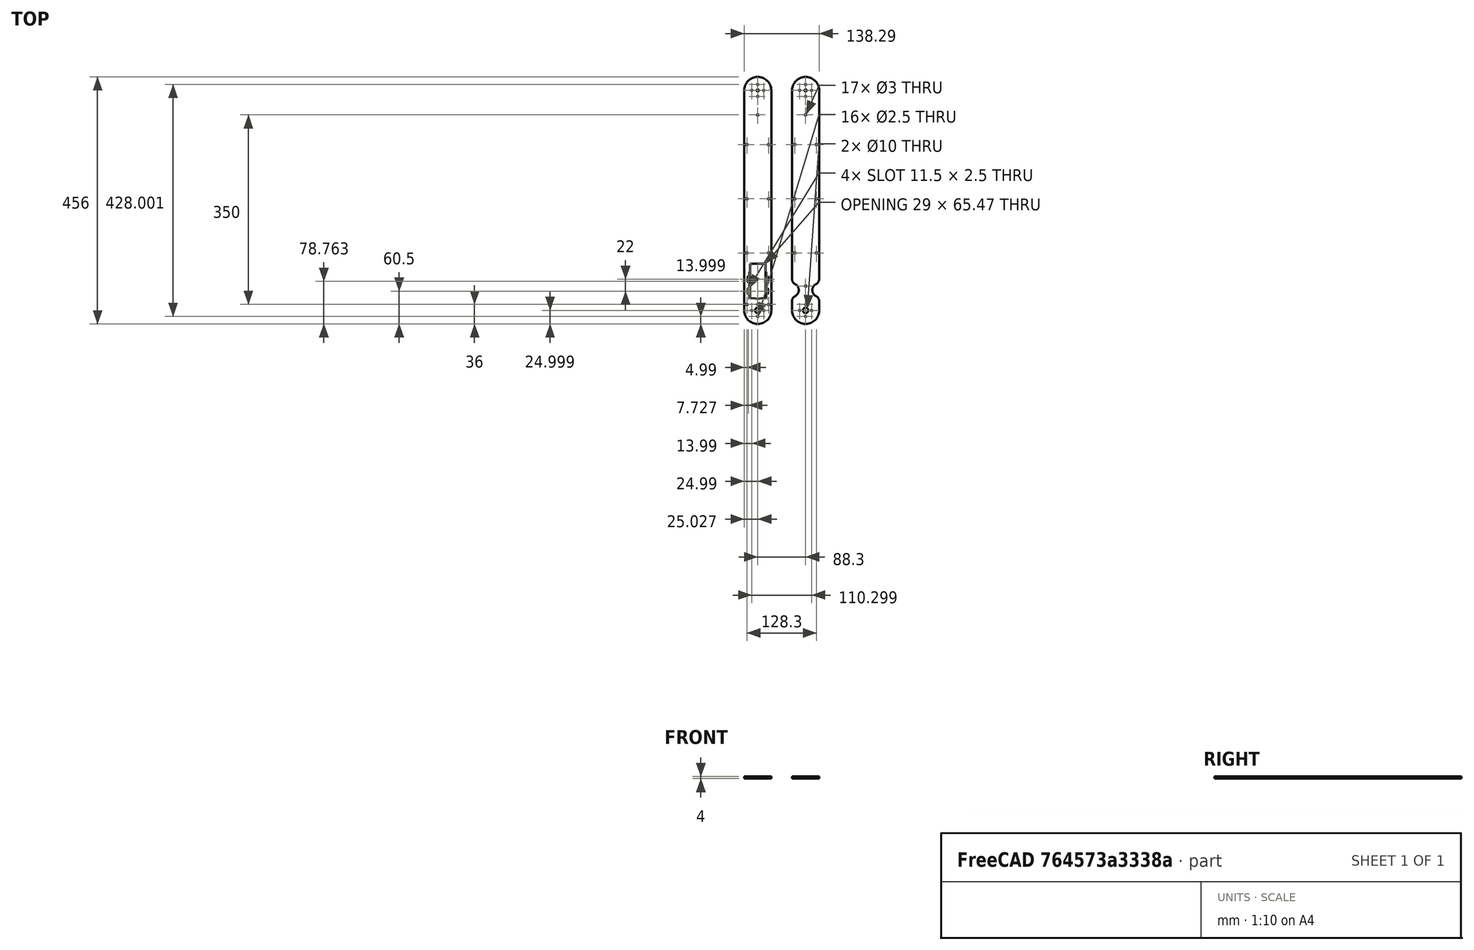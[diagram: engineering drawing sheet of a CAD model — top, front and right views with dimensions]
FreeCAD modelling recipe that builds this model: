
FCSTD DOCUMENT  (FreeCAD 1.0R39109 (Git))
Label: arm_assembly_def3
License: All rights reserved
LicenseURL: https://en.wikipedia.org/wiki/All_rights_reserved
objects: Sketcher::SketchObject×4, PartDesign::Pad×2, PartDesign::Pocket×2, PartDesign::Body×2, Assembly::JointGroup×1, Assembly::AssemblyObject×1, PartDesign::Fillet×1
note: 25 computed .brp shape members not serialized (recipe doc carries the construction recipe); baked Part::Feature solids carry a one-line shape summary decoded from their .brp

FEATURE [Sketcher::SketchObject] Sketch
  ArcFitTolerance = 1e-06
  AttachmentSupport = -> [XY_Plane]
  FullyConstrained = false
  MakeInternals = false
  MapMode = 5
  sketch-geometry (103):
    g0: LineSegment [constr] StartX=1.5008e-12 StartY=20 StartZ=0 EndX=1.5008e-12 EndY=-20 EndZ=0
    g1: LineSegment [constr] StartX=0 StartY=0 StartZ=0 EndX=0 EndY=400 EndZ=0
    g2: LineSegment [constr] StartX=1.5008e-12 StartY=20 StartZ=0 EndX=1.5008e-12 EndY=25 EndZ=0
    g3: Circle CenterX=0 CenterY=400 CenterZ=0 NormalX=0 NormalY=0 NormalZ=1 AngleXU=0 Radius=2
    g4: Circle CenterX=-10.9997 CenterY=400 CenterZ=0 NormalX=0 NormalY=0 NormalZ=1 AngleXU=0 Radius=1.25
    g5: Circle CenterX=0 CenterY=389 CenterZ=0 NormalX=0 NormalY=0 NormalZ=1 AngleXU=0 Radius=1.25
    g6: Circle CenterX=10.9997 CenterY=400 CenterZ=0 NormalX=0 NormalY=0 NormalZ=1 AngleXU=0 Radius=1.25
    g7: Circle CenterX=0 CenterY=411 CenterZ=0 NormalX=0 NormalY=0 NormalZ=1 AngleXU=0 Radius=1.25
    g8: LineSegment [constr] StartX=0 StartY=-5 StartZ=0 EndX=0 EndY=5.99996 EndZ=0
    g9: LineSegment [constr] StartX=0 StartY=0 StartZ=0 EndX=25.23 EndY=0 EndZ=0
    g10: LineSegment [constr] StartX=0 StartY=0 StartZ=0 EndX=-25 EndY=0 EndZ=0
    g11: LineSegment [constr] StartX=20.1368 StartY=86.1259 StartZ=0 EndX=20.1368 EndY=25.0259 EndZ=0
    g12: LineSegment [constr] StartX=0.036848 StartY=80.5 StartZ=0 EndX=14.5368 EndY=80.5 EndZ=0
    g13: LineSegment StartX=14.5368 StartY=80.5 StartZ=0 EndX=-14.4632 EndY=80.5 EndZ=0
    g14: LineSegment StartX=14.5368 StartY=80.5 StartZ=0 EndX=14.5368 EndY=25.0259 EndZ=0
    g15: Circle [constr] CenterX=17.3368 CenterY=78 CenterZ=0 NormalX=0 NormalY=0 NormalZ=1 AngleXU=0 Radius=1.25
    g16: LineSegment [constr] StartX=-20.0632 StartY=86.1259 StartZ=0 EndX=20.1368 EndY=86.1259 EndZ=0
    g17: Circle [constr] CenterX=17.3368 CenterY=56.0002 CenterZ=0 NormalX=0 NormalY=0 NormalZ=1 AngleXU=0 Radius=1.25
    g18: Circle [constr] CenterX=17.3368 CenterY=34 CenterZ=0 NormalX=0 NormalY=0 NormalZ=1 AngleXU=0 Radius=1.25
    g19: Circle [constr] CenterX=0.0368605 CenterY=38.0259 CenterZ=0 NormalX=0 NormalY=0 NormalZ=1 AngleXU=0 Radius=14
    g20: ArcOfCircle [constr] CenterX=0.0368605 CenterY=38.0259 CenterZ=0 NormalX=0 NormalY=0 NormalZ=1 AngleXU=0 Radius=14 StartAngle=4.33213 EndAngle=5.09264
    g21: LineSegment [constr] StartX=5.23308 StartY=25.0259 StartZ=0 EndX=14.5368 EndY=25.0259 EndZ=0
    g22: LineSegment [constr] StartX=14.5368 StartY=25.0259 StartZ=0 EndX=20.1368 EndY=25.0259 EndZ=0
    g23: LineSegment [constr] StartX=17.3368 StartY=56.0002 StartZ=0 EndX=-17.2632 EndY=56.0002 EndZ=0
    g24: LineSegment [constr] StartX=-20.0632 StartY=25.0259 StartZ=0 EndX=-20.0632 EndY=86.1259 EndZ=0
    g25: LineSegment StartX=-14.4632 StartY=80.5 StartZ=0 EndX=-14.4632 EndY=25.0259 EndZ=0
    g26: Circle [constr] CenterX=-17.2632 CenterY=78 CenterZ=0 NormalX=0 NormalY=0 NormalZ=1 AngleXU=0 Radius=1.25
    g27: Circle [constr] CenterX=-17.2632 CenterY=56.0002 CenterZ=0 NormalX=0 NormalY=0 NormalZ=1 AngleXU=0 Radius=1.25
    g28: Circle [constr] CenterX=-17.2632 CenterY=34 CenterZ=0 NormalX=0 NormalY=0 NormalZ=1 AngleXU=0 Radius=1.25
    g29: LineSegment [constr] StartX=-14.4632 StartY=25.0259 StartZ=0 EndX=-5.15937 EndY=25.0259 EndZ=0
    g30: LineSegment [constr] StartX=-20.0632 StartY=25.0259 StartZ=0 EndX=-14.4632 EndY=25.0259 EndZ=0
    g31: LineSegment [constr] StartX=25.23 StartY=199.98 StartZ=0 EndX=-25 EndY=199.98 EndZ=0
    g32: LineSegment [constr] StartX=25.23 StartY=199.98 StartZ=0 EndX=55.23 EndY=199.98 EndZ=0
    g33: LineSegment [constr] StartX=25.23 StartY=0 StartZ=0 EndX=55.23 EndY=0 EndZ=0
    g34: LineSegment [constr] StartX=55.23 StartY=0 StartZ=0 EndX=55.23 EndY=199.98 EndZ=0
    g35: LineSegment [constr] StartX=55.23 StartY=99.9898 StartZ=0 EndX=25.23 EndY=99.9898 EndZ=0
    g36: LineSegment [constr] StartX=25.23 StartY=99.9898 StartZ=0 EndX=-25 EndY=99.9898 EndZ=0
    g37: LineSegment [constr] StartX=25.23 StartY=399.959 StartZ=0 EndX=55.23 EndY=399.959 EndZ=0
    g38: LineSegment [constr] StartX=55.23 StartY=399.959 StartZ=0 EndX=55.23 EndY=199.98 EndZ=0
    g39: LineSegment [constr] StartX=55.23 StartY=299.969 StartZ=0 EndX=25.23 EndY=299.969 EndZ=0
    g40: LineSegment [constr] StartX=25.23 StartY=299.969 StartZ=0 EndX=-25 EndY=299.969 EndZ=0
    g41: LineSegment [constr] StartX=-25 StartY=299.969 StartZ=0 EndX=-20 EndY=299.969 EndZ=0
    g42: LineSegment [constr] StartX=-20 StartY=299.969 StartZ=0 EndX=-20 EndY=199.98 EndZ=0
    g43: LineSegment [constr] StartX=-20 StartY=199.98 StartZ=0 EndX=-20 EndY=99.9898 EndZ=0
    g44: LineSegment [constr] StartX=25.23 StartY=299.969 StartZ=0 EndX=20.23 EndY=299.969 EndZ=0
    g45: LineSegment [constr] StartX=20.23 StartY=299.969 StartZ=0 EndX=20.23 EndY=199.98 EndZ=0
    g46: LineSegment [constr] StartX=20.23 StartY=199.98 StartZ=0 EndX=20.23 EndY=99.9898 EndZ=0
    g47: Circle CenterX=-20 CenterY=299.969 CenterZ=0 NormalX=0 NormalY=0 NormalZ=1 AngleXU=0 Radius=1.5
    g48: Circle CenterX=20.23 CenterY=299.969 CenterZ=0 NormalX=0 NormalY=0 NormalZ=1 AngleXU=0 Radius=1.5
    g49: Circle CenterX=-20 CenterY=199.98 CenterZ=0 NormalX=0 NormalY=0 NormalZ=1 AngleXU=0 Radius=1.5
    g50: Circle CenterX=20.23 CenterY=199.98 CenterZ=0 NormalX=0 NormalY=0 NormalZ=1 AngleXU=0 Radius=1.5
    g51: Circle CenterX=-20 CenterY=99.9898 CenterZ=0 NormalX=0 NormalY=0 NormalZ=1 AngleXU=0 Radius=1.5
    g52: Circle CenterX=20.23 CenterY=99.9898 CenterZ=0 NormalX=0 NormalY=0 NormalZ=1 AngleXU=0 Radius=1.5
    g53: LineSegment [constr] StartX=-17.2632 StartY=34 StartZ=0 EndX=17.3368 EndY=34 EndZ=0
    g54: LineSegment [constr] StartX=-17.2632 StartY=34 StartZ=0 EndX=-17.2632 EndY=25 EndZ=0
    g55: LineSegment [constr] StartX=17.3368 StartY=34 StartZ=0 EndX=17.3368 EndY=25 EndZ=0
    g56: LineSegment [constr] StartX=-17.2632 StartY=78 StartZ=0 EndX=17.3368 EndY=78 EndZ=0
    g57: LineSegment [constr] StartX=-17.2632 StartY=78 StartZ=0 EndX=-17.2632 EndY=69 EndZ=0
    g58: LineSegment [constr] StartX=17.3368 StartY=78 StartZ=0 EndX=17.3368 EndY=69 EndZ=0
    g59: LineSegment StartX=-14.4632 StartY=25.0259 StartZ=0 EndX=-14.4632 EndY=22.0259 EndZ=0
    g60: LineSegment StartX=14.5368 StartY=25.0259 StartZ=0 EndX=14.5368 EndY=22.0259 EndZ=0
    g61: LineSegment [constr] StartX=-17.2632 StartY=56.0002 StartZ=0 EndX=-17.2632 EndY=47.0002 EndZ=0
    g62: LineSegment [constr] StartX=17.3368 StartY=56.0002 StartZ=0 EndX=17.3368 EndY=47.0002 EndZ=0
    g63: Circle [constr] CenterX=0.010165 CenterY=399.952 CenterZ=0 NormalX=0 NormalY=0 NormalZ=1 AngleXU=0 Radius=25.1076
    g64: LineSegment [constr] StartX=0 StartY=400 StartZ=0 EndX=0 EndY=374.844 EndZ=0
    g65: LineSegment [constr] StartX=0 StartY=374.844 StartZ=0 EndX=0 EndY=364.844 EndZ=0
    g66: Circle [constr] CenterX=0 CenterY=364.844 CenterZ=0 NormalX=0 NormalY=0 NormalZ=1 AngleXU=0 Radius=1.5
    g67: Circle [constr] CenterX=-17.2632 CenterY=69 CenterZ=0 NormalX=0 NormalY=0 NormalZ=1 AngleXU=0 Radius=1.25
    g68: Circle [constr] CenterX=17.3368 CenterY=69 CenterZ=0 NormalX=0 NormalY=0 NormalZ=1 AngleXU=0 Radius=1.25
    g69: ArcOfCircle CenterX=-17.2632 CenterY=56.0002 CenterZ=0 NormalX=0 NormalY=0 NormalZ=1 AngleXU=0 Radius=1.25 StartAngle=3.144e-13 EndAngle=3.14159
    g70: ArcOfCircle CenterX=-17.2632 CenterY=47.0002 CenterZ=0 NormalX=0 NormalY=0 NormalZ=1 AngleXU=0 Radius=1.25 StartAngle=3.14159 EndAngle=6.28319
    g71: LineSegment StartX=-16.0132 StartY=56.0002 StartZ=0 EndX=-16.0132 EndY=47.0002 EndZ=0
    g72: LineSegment StartX=-18.5132 StartY=56.0002 StartZ=0 EndX=-18.5132 EndY=47.0002 EndZ=0
    g73: ArcOfCircle CenterX=17.3368 CenterY=34 CenterZ=0 NormalX=0 NormalY=0 NormalZ=1 AngleXU=0 Radius=1.25 StartAngle=6e-16 EndAngle=3.14159
    g74: ArcOfCircle CenterX=17.3368 CenterY=25 CenterZ=0 NormalX=0 NormalY=0 NormalZ=1 AngleXU=0 Radius=1.25 StartAngle=3.14159 EndAngle=6.28319
    g75: LineSegment StartX=18.5868 StartY=34 StartZ=0 EndX=18.5868 EndY=25 EndZ=0
    g76: LineSegment StartX=16.0868 StartY=34 StartZ=0 EndX=16.0868 EndY=25 EndZ=0
    g77: LineSegment StartX=5.233 StartY=16.0259 StartZ=0 EndX=14.5368 EndY=16.0259 EndZ=0
    g78: ArcOfCircle CenterX=0.036848 CenterY=29.0259 CenterZ=0 NormalX=0 NormalY=0 NormalZ=1 AngleXU=0 Radius=14 StartAngle=4.33214 EndAngle=5.09264
    g79: LineSegment StartX=-5.15931 StartY=16.0259 StartZ=0 EndX=-14.4632 EndY=16.0259 EndZ=0
    g80: LineSegment StartX=-14.4632 StartY=22.0259 StartZ=0 EndX=-14.4632 EndY=16.0259 EndZ=0
    g81: LineSegment StartX=14.5368 StartY=22.0259 StartZ=0 EndX=14.5368 EndY=16.0259 EndZ=0
    g82: ArcOfCircle CenterX=17.3368 CenterY=56.0002 CenterZ=0 NormalX=0 NormalY=0 NormalZ=1 AngleXU=0 Radius=1.25 StartAngle=8.3e-15 EndAngle=3.14159
    g83: ArcOfCircle CenterX=17.3368 CenterY=47.0002 CenterZ=0 NormalX=0 NormalY=0 NormalZ=1 AngleXU=0 Radius=1.25 StartAngle=3.14159 EndAngle=6.28319
    g84: LineSegment StartX=18.5868 StartY=56.0002 StartZ=0 EndX=18.5868 EndY=47.0002 EndZ=0
    g85: LineSegment StartX=16.0868 StartY=56.0002 StartZ=0 EndX=16.0868 EndY=47.0002 EndZ=0
    g86: ArcOfCircle CenterX=-17.2632 CenterY=34 CenterZ=0 NormalX=0 NormalY=0 NormalZ=1 AngleXU=0 Radius=1.25 StartAngle=1e-16 EndAngle=3.14159
    g87: ArcOfCircle CenterX=-17.2632 CenterY=25 CenterZ=0 NormalX=0 NormalY=0 NormalZ=1 AngleXU=0 Radius=1.25 StartAngle=3.14159 EndAngle=6.28319
    g88: LineSegment StartX=-16.0132 StartY=34 StartZ=0 EndX=-16.0132 EndY=25 EndZ=0
    g89: LineSegment StartX=-18.5132 StartY=34 StartZ=0 EndX=-18.5132 EndY=25 EndZ=0
    g90: Circle [constr] CenterX=0 CenterY=-6 CenterZ=0 NormalX=0 NormalY=0 NormalZ=1 AngleXU=0 Radius=14
    g91: Circle [constr] CenterX=0.010165 CenterY=-5.99291 CenterZ=0 NormalX=0 NormalY=0 NormalZ=1 AngleXU=0 Radius=11
    g92: Circle CenterX=0 CenterY=-6 CenterZ=0 NormalX=0 NormalY=0 NormalZ=1 AngleXU=0 Radius=5
    g93: Circle CenterX=0 CenterY=-16.9997 CenterZ=0 NormalX=0 NormalY=0 NormalZ=1 AngleXU=0 Radius=1.25
    g94: Circle CenterX=10.9997 CenterY=-6 CenterZ=0 NormalX=0 NormalY=0 NormalZ=1 AngleXU=0 Radius=1.25
    g95: Circle CenterX=-10.9997 CenterY=-6 CenterZ=0 NormalX=0 NormalY=0 NormalZ=1 AngleXU=0 Radius=1.25
    g96: Circle CenterX=0 CenterY=4.99996 CenterZ=0 NormalX=0 NormalY=0 NormalZ=1 AngleXU=0 Radius=1.25
    g97: ArcOfCircle CenterX=0.010165 CenterY=-5.99291 CenterZ=0 NormalX=0 NormalY=0 NormalZ=1 AngleXU=0 Radius=25 StartAngle=3.14159 EndAngle=6.28319
    g98: ArcOfCircle CenterX=0.010165 CenterY=399.952 CenterZ=0 NormalX=0 NormalY=0 NormalZ=1 AngleXU=0 Radius=25 StartAngle=0 EndAngle=3.14159
    g99: LineSegment StartX=-24.9898 StartY=-5.99291 StartZ=0 EndX=-24.9898 EndY=399.952 EndZ=0
    g100: LineSegment StartX=25.0102 StartY=-5.99291 StartZ=0 EndX=25.0102 EndY=399.952 EndZ=0
    g101: LineSegment [constr] StartX=0 StartY=364.844 StartZ=0 EndX=0 EndY=354.844 EndZ=0
    g102: Circle CenterX=0 CenterY=354.844 CenterZ=0 NormalX=0 NormalY=0 NormalZ=1 AngleXU=0 Radius=1.5
  constraints (212):
    c: Vertical(g0)
    c: Vertical(g1)
    c: Coincident(g2,g0)
    c: Vertical(g2)
    c: Diameter(g3) = 4
    c: Coincident(g3,g1)
    c: Diameter(g7) = 2.5
    c: Diameter(g4) = 2.5
    c: Diameter(g5) = 2.5
    c: Diameter(g6) = 2.5
    c: Vertical(g8)
    c: Horizontal(g10)
    c: Horizontal(g9)
    c: Coincident(g16,g11)
    c: Coincident(g24,g16)
    c: Horizontal(g16)
    c: Vertical(g11)
    c: Vertical(g24)
    c: Distance(g11,g24) = 40.2
    c: Distance(g16,g24) = 61.1
    c: Diameter(g20) = 28
    c: Horizontal(g12)
    c: Coincident(g13,g12)
    c: Horizontal(g13)
    c: Coincident(g25,g13)
    c: Vertical(g25)
    c: Coincident(g14,g12)
    c: Vertical(g14)
    c: Coincident(g19,g20)
    c: PointOnObject(g20,g19)
    c: Coincident(g21,g20)
    c: Coincident(g21,g14)
    c: Horizontal(g21)
    c: Coincident(g22,g14)
    c: Coincident(g22,g11)
    c: Horizontal(g22)
    c: Coincident(g29,g25)
    c: Coincident(g29,g20)
    c: Horizontal(g29)
    c: Coincident(g30,g24)
    c: Coincident(g30,g25)
    c: Horizontal(g30)
    c: Coincident(g23,g17)
    c: Coincident(g23,g27)
    c: Horizontal(g23)
    c: DistanceY(g19,g1) = 361.974
    c: Horizontal(g31)
    c: Distance(g32) = 30
    c: Horizontal(g32)
    c: Coincident(g32,g31)
    c: Distance(g33) = 30
    c: Horizontal(g33)
    c: Coincident(g33,g9)
    c: PointOnObject(g33,g-1)
    c: Coincident(g34,g33)
    c: Coincident(g34,g32)
    c: Vertical(g34)
    c: Symmetric(g34,g34,g35)
    c: Horizontal(g35)
    c: Coincident(g36,g35)
    c: Horizontal(g36)
    c: Distance(g37) = 30
    c: Horizontal(g37)
    c: Coincident(g38,g37)
    c: Coincident(g38,g32)
    c: Symmetric(g38,g38,g39)
    c: Horizontal(g39)
    c: Coincident(g40,g39)
    c: Horizontal(g40)
    c: Distance(g41) = 5
    c: Coincident(g41,g40)
    c: PointOnObject(g41,g40)
    c: Coincident(g42,g41)
    c: PointOnObject(g42,g31)
    c: Vertical(g42)
    c: Coincident(g43,g42)
    c: PointOnObject(g43,g36)
    c: Vertical(g43)
    c: Distance(g44) = 5
    c: Coincident(g44,g39)
    c: PointOnObject(g44,g40)
    c: Coincident(g45,g44)
    c: PointOnObject(g45,g31)
    c: Vertical(g45)
    c: Coincident(g46,g45)
    c: PointOnObject(g46,g36)
    c: Vertical(g46)
    c: Coincident(g47,g41)
    c: Diameter(g47) = 3
    c: Coincident(g48,g44)
    c: Equal(g47,g48)
    c: Coincident(g49,g42)
    c: Equal(g47,g49)
    c: Coincident(g50,g45)
    c: Equal(g49,g50)
    c: Coincident(g51,g43)
    c: Equal(g49,g51)
    c: Coincident(g52,g46)
    c: Equal(g51,g52)
    c: Coincident(g53,g28)
    c: Coincident(g53,g18)
    c: Horizontal(g53)
    c: DistanceX(g53,g53) = 34.6
    c: Coincident(g54,g28)
    c: Vertical(g54)
    c: Coincident(g55,g18)
    c: Vertical(g55)
    c: Coincident(g56,g26)
    c: Coincident(g56,g15)
    c: Horizontal(g56)
    c: DistanceX(g56,g56) = 34.6
    c: Distance(g57) = 9
    c: Coincident(g57,g26)
    c: Vertical(g57)
    c: Coincident(g58,g15)
    c: Vertical(g58)
    c: DistanceX(g25,g14) = 29
    c: Distance(g59) = 3
    c: Coincident(g59,g25)
    c: Vertical(g59)
    c: Coincident(g60,g14)
    c: Vertical(g60)
    c: DistanceX(g23,g23) = 34.6
    c: Coincident(g61,g23)
    c: Vertical(g61)
    c: Coincident(g62,g17)
    c: Vertical(g62)
    c: DistanceX(g1) = 0
    c: DistanceY(g1) = 400
    c: Coincident(g64,g1)
    c: PointOnObject(g64,g63)
    c: Vertical(g64)
    c: Distance(g65) = 10
    c: Coincident(g65,g64)
    c: PointOnObject(g65,g1)
    c: Diameter(g66) = 3
    c: Coincident(g66,g65)
    c: DistanceX(g26) = -17.2632
    c: DistanceY(g26) = 78
    c: DistanceX(g23) = -17.2632
    c: DistanceY(g23) = 56.0002
    c: Equal(g58,g57)
    c: Equal(g61,g57)
    c: Equal(g62,g61)
    c: DistanceX(g28) = -17.2632
    c: DistanceY(g28) = 34
    c: Equal(g54,g61)
    c: Equal(g55,g54)
    c: Equal(g60,g59)
    c: Coincident(g67,g57)
    c: Equal(g67,g26)
    c: Coincident(g68,g58)
    c: Equal(g68,g15)
    c: Tangent(g69,g71) = 1.5708
    c: Tangent(g69,g72) = -1.5708
    c: Tangent(g70,g71) = 1.5708
    c: Tangent(g70,g72) = -1.5708
    c: Equal(g69,g70)
    c: Coincident(g69,g23)
    c: Coincident(g70,g61)
    c: Equal(g27,g69)
    c: Tangent(g73,g75) = 1.5708
    c: Tangent(g73,g76) = -1.5708
    c: Tangent(g74,g75) = 1.5708
    c: Tangent(g74,g76) = -1.5708
    c: Equal(g73,g74)
    c: Radius(g73) = 1.25
    c: Coincident(g73,g18)
    c: Coincident(g74,g55)
    c: Diameter(g78) = 28
    c: Coincident(g77,g78)
    c: Horizontal(g77)
    c: Coincident(g79,g78)
    c: Horizontal(g79)
    c: Coincident(g80,g59)
    c: Coincident(g80,g79)
    c: Vertical(g80)
    c: Coincident(g81,g60)
    c: Coincident(g81,g77)
    c: Vertical(g81)
    c: Tangent(g82,g84) = 1.5708
    c: Tangent(g82,g85) = -1.5708
    c: Tangent(g83,g84) = 1.5708
    c: Tangent(g83,g85) = -1.5708
    c: Equal(g82,g83)
    c: Tangent(g86,g88) = 1.5708
    c: Tangent(g86,g89) = -1.5708
    c: Tangent(g87,g88) = 1.5708
    c: Tangent(g87,g89) = -1.5708
    c: Equal(g86,g87)
    c: Diameter(g90) = 28
    c: Diameter(g91) = 22
    c: Diameter(g92) = 10
    c: Coincident(g92,g90)
    c: Diameter(g96) = 2.5
    c: Diameter(g95) = 2.5
    c: Diameter(g93) = 2.5
    c: Diameter(g94) = 2.5
    c: Tangent(g97,g99) = 1.5708
    c: Tangent(g97,g100) = -1.5708
    c: Tangent(g98,g99) = 1.5708
    c: Tangent(g98,g100) = -1.5708
    c: Equal(g97,g98)
    c: Vertical(g100)
    c: Radius(g97) = 25
    c: Coincident(g97,g91)
    c: Coincident(g98,g63)
    c: Distance(g101) = 10
    c: Coincident(g101,g65)
    c: PointOnObject(g101,g1)
    c: Coincident(g102,g101)
    c: Equal(g102,g66)
FEATURE [Sketcher::SketchObject] Sketch001
  ArcFitTolerance = 1e-06
  FullyConstrained = false
  MakeInternals = false
  MapMode = 5
  sketch-geometry (50):
    g0: Circle [constr] CenterX=0 CenterY=0.000303 CenterZ=0 NormalX=0 NormalY=0 NormalZ=1 AngleXU=0 Radius=14
    g1: Circle CenterX=0 CenterY=0.000303 CenterZ=0 NormalX=0 NormalY=0 NormalZ=1 AngleXU=0 Radius=2
    g2: Circle [constr] CenterX=0 CenterY=0 CenterZ=0 NormalX=0 NormalY=0 NormalZ=1 AngleXU=0 Radius=11
    g3: Circle CenterX=10.9997 CenterY=0.000303 CenterZ=0 NormalX=0 NormalY=0 NormalZ=1 AngleXU=0 Radius=1.25
    g4: Circle CenterX=0 CenterY=11 CenterZ=0 NormalX=0 NormalY=0 NormalZ=1 AngleXU=0 Radius=1.25
    g5: Circle CenterX=-10.9997 CenterY=0.000303 CenterZ=0 NormalX=0 NormalY=0 NormalZ=1 AngleXU=0 Radius=1.25
    g6: Circle CenterX=0 CenterY=-10.9994 CenterZ=0 NormalX=0 NormalY=0 NormalZ=1 AngleXU=0 Radius=1.25
    g7: LineSegment [constr] StartX=25 StartY=200 StartZ=0 EndX=-25 EndY=200 EndZ=0
    g8: LineSegment [constr] StartX=25 StartY=200 StartZ=0 EndX=55 EndY=200 EndZ=0
    g9: LineSegment [constr] StartX=25 StartY=0 StartZ=0 EndX=55 EndY=0 EndZ=0
    g10: LineSegment [constr] StartX=55 StartY=200 StartZ=0 EndX=55 EndY=0 EndZ=0
    g11: LineSegment [constr] StartX=55 StartY=100 StartZ=0 EndX=25 EndY=100 EndZ=0
    g12: LineSegment [constr] StartX=25 StartY=100 StartZ=0 EndX=-25 EndY=100 EndZ=0
    g13: LineSegment [constr] StartX=55 StartY=300 StartZ=0 EndX=25 EndY=300 EndZ=0
    g14: LineSegment [constr] StartX=25 StartY=300 StartZ=0 EndX=-25 EndY=300 EndZ=0
    g15: LineSegment [constr] StartX=-25 StartY=300 StartZ=0 EndX=-20 EndY=300 EndZ=0
    g16: LineSegment [constr] StartX=-20 StartY=300 StartZ=0 EndX=-20 EndY=200 EndZ=0
    g17: LineSegment [constr] StartX=-20 StartY=200 StartZ=0 EndX=-20 EndY=100 EndZ=0
    g18: LineSegment [constr] StartX=25 StartY=100 StartZ=0 EndX=20 EndY=100 EndZ=0
    g19: LineSegment [constr] StartX=20 StartY=100 StartZ=0 EndX=20 EndY=200 EndZ=0
    g20: LineSegment [constr] StartX=20 StartY=200 StartZ=0 EndX=20 EndY=300 EndZ=0
    g21: Circle CenterX=-20 CenterY=300 CenterZ=0 NormalX=0 NormalY=0 NormalZ=1 AngleXU=0 Radius=1.5
    g22: Circle CenterX=20 CenterY=300 CenterZ=0 NormalX=0 NormalY=0 NormalZ=1 AngleXU=0 Radius=1.5
    g23: Circle CenterX=-20 CenterY=200 CenterZ=0 NormalX=0 NormalY=0 NormalZ=1 AngleXU=0 Radius=1.5
    g24: Circle CenterX=20 CenterY=200 CenterZ=0 NormalX=0 NormalY=0 NormalZ=1 AngleXU=0 Radius=1.5
    g25: Circle CenterX=-20 CenterY=100 CenterZ=0 NormalX=0 NormalY=0 NormalZ=1 AngleXU=0 Radius=1.5
    g26: Circle CenterX=20 CenterY=100 CenterZ=0 NormalX=0 NormalY=0 NormalZ=1 AngleXU=0 Radius=1.5
    g27: Circle [constr] CenterX=0 CenterY=0 CenterZ=0 NormalX=0 NormalY=0 NormalZ=1 AngleXU=0 Radius=25
    g28: LineSegment [constr] StartX=0 StartY=0 StartZ=0 EndX=0 EndY=25 EndZ=0
    g29: LineSegment [constr] StartX=0 StartY=25 StartZ=0 EndX=0 EndY=35 EndZ=0
    g30: Circle [constr] CenterX=0 CenterY=35 CenterZ=0 NormalX=0 NormalY=0 NormalZ=1 AngleXU=0 Radius=1.5
    g31: LineSegment [constr] StartX=0 StartY=35 StartZ=0 EndX=0 EndY=45 EndZ=0
    g32: Circle CenterX=0 CenterY=45 CenterZ=0 NormalX=0 NormalY=0 NormalZ=1 AngleXU=0 Radius=1.5
    g33: Circle CenterX=0 CenterY=406.001 CenterZ=0 NormalX=0 NormalY=0 NormalZ=1 AngleXU=0 Radius=5
    g34: Circle CenterX=0 CenterY=417.001 CenterZ=0 NormalX=0 NormalY=0 NormalZ=1 AngleXU=0 Radius=1.25
    g35: Circle CenterX=-10.9997 CenterY=406.001 CenterZ=0 NormalX=0 NormalY=0 NormalZ=1 AngleXU=0 Radius=1.25
    g36: Circle CenterX=0 CenterY=395.001 CenterZ=0 NormalX=0 NormalY=0 NormalZ=1 AngleXU=0 Radius=1.25
    g37: LineSegment [constr] StartX=0 StartY=6.0003 StartZ=0 EndX=0 EndY=406.001 EndZ=0
    g38: Circle CenterX=10.9997 CenterY=406.001 CenterZ=0 NormalX=0 NormalY=0 NormalZ=1 AngleXU=0 Radius=1.25
    g39: LineSegment [constr] StartX=25 StartY=406.001 StartZ=0 EndX=55 EndY=406.001 EndZ=0
    g40: Circle [constr] CenterX=0 CenterY=406.001 CenterZ=0 NormalX=0 NormalY=0 NormalZ=1 AngleXU=0 Radius=25
    g41: LineSegment [constr] StartX=0 StartY=406.001 StartZ=0 EndX=0 EndY=381.001 EndZ=0
    g42: LineSegment [constr] StartX=0 StartY=381.001 StartZ=0 EndX=0 EndY=371.001 EndZ=0
    g43: Circle [constr] CenterX=0 CenterY=371.001 CenterZ=0 NormalX=0 NormalY=0 NormalZ=1 AngleXU=0 Radius=1.5
    g44: LineSegment [constr] StartX=0 StartY=371.001 StartZ=0 EndX=0 EndY=361.001 EndZ=0
    g45: Circle CenterX=0 CenterY=361.001 CenterZ=0 NormalX=0 NormalY=0 NormalZ=1 AngleXU=0 Radius=1.5
    g46: ArcOfCircle CenterX=0 CenterY=0 CenterZ=0 NormalX=0 NormalY=0 NormalZ=1 AngleXU=0 Radius=25 StartAngle=3.14159 EndAngle=6.28319
    g47: ArcOfCircle CenterX=0 CenterY=406.001 CenterZ=0 NormalX=0 NormalY=0 NormalZ=1 AngleXU=0 Radius=25 StartAngle=0 EndAngle=3.14159
    g48: LineSegment StartX=-25 StartY=6.97e-14 StartZ=0 EndX=-25 EndY=406.001 EndZ=0
    g49: LineSegment StartX=25 StartY=-6.1e-15 StartZ=0 EndX=25 EndY=406.001 EndZ=0
  constraints (91):
    c: Diameter(g0) = 28
    c: Diameter(g1) = 4
    c: Coincident(g1,g0)
    c: Diameter(g2) = 22
    c: Diameter(g4) = 2.5
    c: Diameter(g5) = 2.5
    c: Diameter(g6) = 2.5
    c: Diameter(g3) = 2.5
    c: Distance(g8) = 30
    c: Horizontal(g8)
    c: Coincident(g8,g7)
    c: Distance(g9) = 30
    c: Horizontal(g9)
    c: PointOnObject(g9,g-1)
    c: Coincident(g10,g8)
    c: Coincident(g10,g9)
    c: Symmetric(g10,g10,g11)
    c: Horizontal(g11)
    c: Coincident(g12,g11)
    c: Horizontal(g12)
    c: Horizontal(g13)
    c: Coincident(g14,g13)
    c: Horizontal(g14)
    c: Distance(g15) = 5
    c: Horizontal(g15)
    c: Coincident(g15,g14)
    c: Coincident(g16,g15)
    c: PointOnObject(g16,g7)
    c: Vertical(g16)
    c: Coincident(g17,g16)
    c: PointOnObject(g17,g12)
    c: Vertical(g17)
    c: Distance(g18) = 5
    c: Horizontal(g18)
    c: Coincident(g18,g11)
    c: Coincident(g19,g18)
    c: PointOnObject(g19,g7)
    c: Vertical(g19)
    c: Coincident(g20,g19)
    c: PointOnObject(g20,g14)
    c: Vertical(g20)
    c: Diameter(g21) = 3
    c: Coincident(g21,g15)
    c: Coincident(g22,g20)
    c: Equal(g21,g22)
    c: Coincident(g23,g16)
    c: Equal(g21,g23)
    c: Coincident(g24,g19)
    c: Equal(g23,g24)
    c: Coincident(g25,g17)
    c: Equal(g23,g25)
    c: Coincident(g26,g18)
    c: Equal(g25,g26)
    c: DistanceX(g2) = 0
    c: DistanceY(g2) = 0
    c: Coincident(g28,g2)
    c: PointOnObject(g28,g27)
    c: Vertical(g28)
    c: Distance(g29) = 10
    c: Coincident(g29,g28)
    c: Diameter(g30) = 3
    c: Coincident(g30,g29)
    c: Distance(g31) = 10
    c: Coincident(g31,g29)
    c: Coincident(g32,g31)
    c: Equal(g32,g30)
    c: Vertical(g37)
    c: Coincident(g33,g37)
    c: Diameter(g34) = 2.5
    c: Diameter(g35) = 2.5
    c: Diameter(g36) = 2.5
    c: Diameter(g38) = 2.5
    c: Horizontal(g39)
    c: Coincident(g40,g37)
    c: Coincident(g41,g37)
    c: PointOnObject(g41,g40)
    c: Vertical(g41)
    c: Coincident(g42,g41)
    c: PointOnObject(g42,g37)
    c: Coincident(g44,g42)
    c: Vertical(g44)
    c: Coincident(g45,g44)
    c: Tangent(g46,g48) = 1.5708
    c: Tangent(g46,g49) = -1.5708
    c: Tangent(g47,g48) = 1.5708
    c: Tangent(g47,g49) = -1.5708
    c: Equal(g46,g47)
    c: Vertical(g49)
    c: Radius(g46) = 25
    c: Coincident(g46,g27)
    c: Coincident(g47,g33)
FEATURE [PartDesign::Pad] Pad
  Direction = (0,0,1)
  Length = 4
  Length2 = 10
  Profile = -> Sketch
  ReferenceAxis = -> Sketch [N_Axis]
  Refine = true
  Suppressed = false
  Type = 0
FEATURE [PartDesign::Pad] Pad001
  Direction = (0,0,1)
  Length = 4
  Length2 = 10
  Profile = -> Sketch001
  ReferenceAxis = -> Sketch001 [N_Axis]
  Refine = true
  Suppressed = false
  Type = 0
FEATURE [Assembly::JointGroup] Joints
FEATURE [Assembly::AssemblyObject] Assembly
  Group = -> [Joints]
  Origin = -> Origin003
  Type = Assembly
FEATURE [Sketcher::SketchObject] Sketch002
  ArcFitTolerance = 1e-06
  AttachmentSupport = -> [Pad001]
  ExternalGeometry = -> [Pad001]
  FullyConstrained = true
  MakeInternals = false
  MapMode = 5
  Placement = pos=(0,0,4) rot=(0,0,1;0rad)
  sketch-geometry (7):
    g0: Circle [constr] CenterX=0 CenterY=406.001 CenterZ=0 NormalX=0 NormalY=0 NormalZ=1 AngleXU=0 Radius=45
    g1: LineSegment [constr] StartX=0 StartY=361.001 StartZ=0 EndX=25 EndY=361.001 EndZ=0
    g2: LineSegment [constr] StartX=25 StartY=361.001 StartZ=0 EndX=25 EndY=368.584 EndZ=0
    g3: LineSegment [constr] StartX=0 StartY=361.001 StartZ=0 EndX=-25 EndY=361.001 EndZ=0
    g4: LineSegment [constr] StartX=-25 StartY=361.001 StartZ=0 EndX=-25 EndY=368.584 EndZ=0
    g5: Circle CenterX=-25 CenterY=368.584 CenterZ=0 NormalX=0 NormalY=0 NormalZ=1 AngleXU=0 Radius=12.5
    g6: Circle CenterX=25 CenterY=368.584 CenterZ=0 NormalX=0 NormalY=0 NormalZ=1 AngleXU=0 Radius=12.5
  constraints (18):
    c: Coincident(g0,g-3)
    c: PointOnObject(g-4,g0)
    c: Coincident(g1,g-4)
    c: PointOnObject(g1,g-6)
    c: Horizontal(g1)
    c: Coincident(g2,g1)
    c: PointOnObject(g2,g0)
    c: Vertical(g2)
    c: Coincident(g3,g1)
    c: PointOnObject(g3,g-5)
    c: Horizontal(g3)
    c: Coincident(g4,g3)
    c: PointOnObject(g4,g0)
    c: Vertical(g4)
    c: Coincident(g5,g4)
    c: Diameter(g5) = 25
    c: Coincident(g6,g2)
    c: Equal(g6,g5)
FEATURE [PartDesign::Pocket] Pocket
  BaseFeature = -> Pad001
  Direction = (0,0,-1)
  Length = 11
  Length2 = 5
  Profile = -> Sketch002
  ReferenceAxis = -> Sketch002 [N_Axis]
  Refine = true
  Suppressed = false
  Type = 0
FEATURE [PartDesign::Fillet] Fillet
  Base = -> Pocket [Edge59,Edge9,Edge61,Edge6]
  BaseFeature = -> Pocket
  Radius = 10
  Refine = true
  SupportTransform = false
  Suppressed = false
  UseAllEdges = false
FEATURE [PartDesign::Body] Body001  label="arm_high_1"
  AllowCompound = false
  Group = -> [Sketch001,Pad001,Sketch002,Pocket,Fillet]
  Origin = -> Origin001
  Placement = pos=(68.48,410,17.66) rot=(0,0,1;3.14159rad)
  Tip = -> Fillet
FEATURE [Sketcher::SketchObject] Sketch003
  ArcFitTolerance = 1e-06
  AttachmentSupport = -> [Pad]
  ExternalGeometry = -> [Pad]
  FullyConstrained = true
  MakeInternals = false
  MapMode = 5
  Placement = pos=(0,0,4) rot=(0,0,1;0rad)
  sketch-geometry (6):
    g0: LineSegment [constr] StartX=20.23 StartY=99.9898 StartZ=0 EndX=20.23 EndY=4.99996 EndZ=0
    g1: LineSegment [constr] StartX=0 StartY=4.99996 StartZ=0 EndX=20.23 EndY=4.99996 EndZ=0
    g2: Circle CenterX=20.23 CenterY=4.99996 CenterZ=0 NormalX=0 NormalY=0 NormalZ=1 AngleXU=0 Radius=1.5
    g3: LineSegment [constr] StartX=-20 StartY=99.9898 StartZ=0 EndX=-20 EndY=4.99996 EndZ=0
    g4: LineSegment [constr] StartX=0 StartY=4.99996 StartZ=0 EndX=-20 EndY=4.99996 EndZ=0
    g5: Circle CenterX=-20 CenterY=4.99996 CenterZ=0 NormalX=0 NormalY=0 NormalZ=1 AngleXU=0 Radius=1.5
  constraints (14):
    c: Coincident(g0,g-3)
    c: Vertical(g0)
    c: Coincident(g1,g-4)
    c: Horizontal(g1)
    c: Coincident(g1,g0)
    c: Coincident(g2,g0)
    c: Diameter(g2) = 3
    c: Coincident(g3,g-5)
    c: Vertical(g3)
    c: Coincident(g4,g1)
    c: Horizontal(g4)
    c: Coincident(g4,g3)
    c: Coincident(g5,g3)
    c: Equal(g5,g2)
FEATURE [PartDesign::Pocket] Pocket001
  BaseFeature = -> Pad
  Direction = (0,0,-1)
  Length = 12
  Length2 = 5
  Profile = -> Sketch003
  ReferenceAxis = -> Sketch003 [N_Axis]
  Refine = true
  Suppressed = false
  Type = 0
FEATURE [PartDesign::Body] Body  label="arm_low_1"
  AllowCompound = false
  Group = -> [Sketch,Pad,Sketch003,Pocket001]
  Origin = -> Origin
  Placement = pos=(-19.82,10,17.66) rot=(0,0,1;0rad)
  Tip = -> Pocket001
